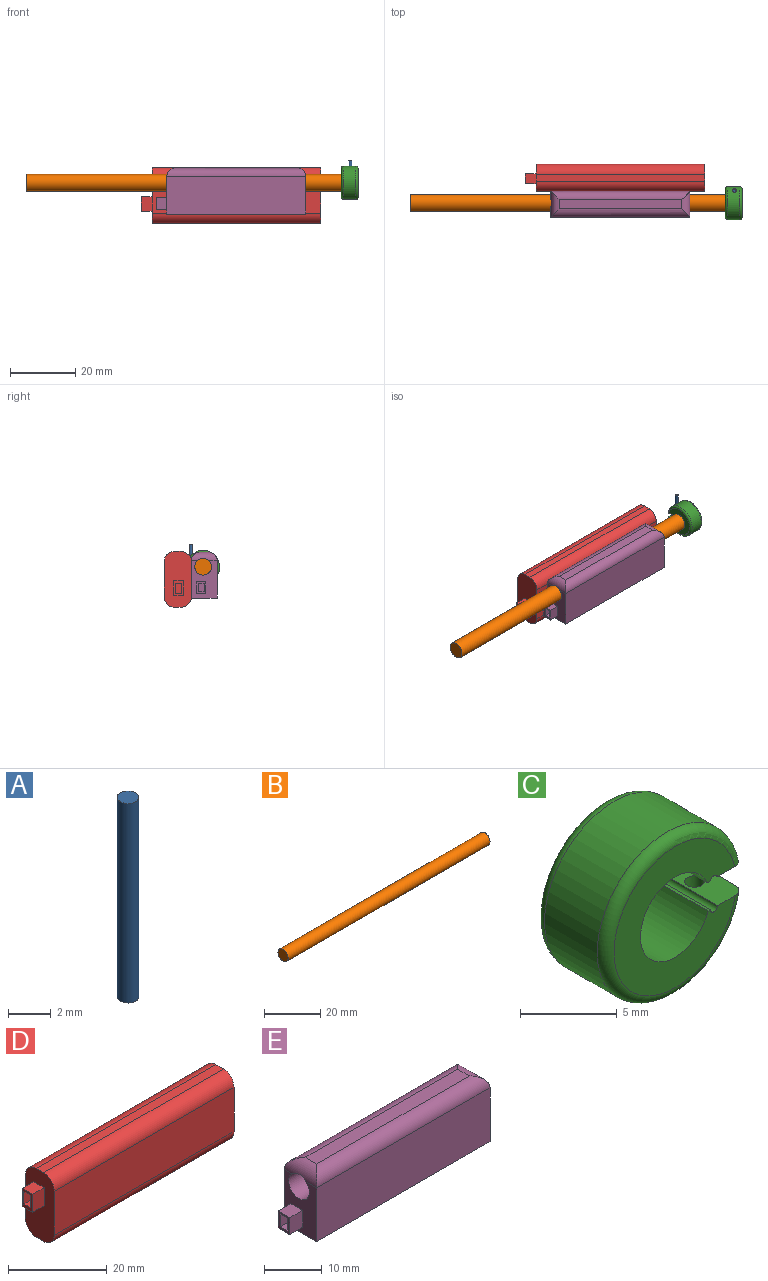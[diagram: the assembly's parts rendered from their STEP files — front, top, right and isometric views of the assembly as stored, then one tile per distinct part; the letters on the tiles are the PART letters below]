
ASSEMBLY  parts=5 mates=4
PART A: 3 faces, bbox 1x1x11.4 mm
  f0: cylinder r=0.51mm len=11.43mm, axis (0,0,-1), area 36.5mm2, adj f1,f2
  f1: plane 1.02x1.02mm, normal (0,0,1), area 0.8mm2, adj f0
  f2: plane 1.02x1.02mm, normal (0,0,-1), area 0.8mm2, adj f0
PART B: 3 faces, bbox 101.6x5.1x5.1 mm
  f0: cylinder r=2.54mm len=101.6mm, axis (-1,0,0), area 1621.5mm2, adj f1,f2
  f1: plane 5.08x5.08mm, normal (1,0,0), area 20.3mm2, adj f0
  f2: plane 5.08x5.08mm, normal (-1,0,0), area 20.3mm2, adj f0
PART C: 15 faces, bbox 10.9x5.1x11 mm
  f0: plane 5.08x1.89mm, normal (0,0,-1), area 8.6mm2, adj f1,f7,f8,f9,f11,f13,f14
  f1: cylinder r=5.08mm len=10.16mm, axis (0,1,0), area 112.8mm2, adj f0,f2,f10,f12,f13,f14
  f2: plane 5.08x1.92mm, normal (0,0,1), area 8.8mm2, adj f1,f3,f8,f9,f10,f13,f14
  f3: cylinder r=0.26mm len=5.08mm, axis (0,1,0), area 4.2mm2, adj f2,f4,f8,f9
  f4: plane 5.08x0.16mm, normal (0,0,1), area 0.8mm2, adj f3,f5,f8,f9
  f5: cylinder r=2.54mm len=5.08mm, axis (0,1,0), area 71.5mm2, adj f4,f6,f8,f9
  f6: plane 5.08x0.24mm, normal (0,0,-1), area 1.2mm2, adj f5,f7,f8,f9
  f7: cylinder r=0.27mm len=5.08mm, axis (0,1,0), area 3.6mm2, adj f0,f6,f8,f9
  f8: plane 8.93x8.86mm, normal (0,-1,0), area 38.6mm2, adj f0,f2,f3,f4,f5,f6,f7,f14
  f9: plane 8.93x8.86mm, normal (0,1,0), area 38.6mm2, adj f0,f2,f3,f4,f5,f6,f7,f13
  f10: cylinder r=0.51mm len=3.07mm, axis (0,0,1), area 8.1mm2, adj f1,f2
  f11: cylinder r=0.51mm len=2.84mm, axis (0,0,1), area 6.9mm2, adj f0,f12
  f12: bspline ~1.55x1.24mm, area 0.8mm2, adj f1,f11
  f13: torus R=4.47mm, axis (0,-1,0), area 27.6mm2, adj f0,f1,f2,f9
  f14: torus R=4.47mm, axis (0,-1,0), area 27.6mm2, adj f0,f1,f2,f8
PART D: 20 faces, bbox 54.9x8.3x17 mm
  f0: plane 17.05x8.27mm, normal (-1,0,0), area 119.4mm2, adj f1,f2,f3,f4,f6,f7,f8,f9
  f1: plane 51.56x2.14mm, normal (0,0,1), area 110.1mm2, adj f0,f5,f6,f9
  f2: plane 51.56x10.91mm, normal (0,-1,0), area 562.7mm2, adj f0,f5,f6,f7
  f3: plane 51.56x2.14mm, normal (0,0,-1), area 110.1mm2, adj f0,f5,f7,f8
  f4: plane 51.56x10.91mm, normal (0,1,0), area 562.7mm2, adj f0,f5,f8,f9
  f5: plane 17.05x8.27mm, normal (1,0,0), area 132.9mm2, adj f1,f2,f3,f4,f6,f7,f8,f9
  f6: cylinder r=3.07mm len=51.56mm, axis (-1,0,0), area 248.3mm2, adj f0,f1,f2,f5
  f7: cylinder r=3.07mm len=51.56mm, axis (1,0,0), area 248.3mm2, adj f0,f2,f3,f5
  f8: cylinder r=3.07mm len=51.56mm, axis (1,0,0), area 248.3mm2, adj f0,f3,f4,f5
  f9: cylinder r=3.07mm len=51.56mm, axis (-1,0,0), area 248.3mm2, adj f0,f1,f4,f5
  f10: plane 3.35x3.01mm, normal (0,0,-1), area 10.1mm2, adj f0,f11,f17,f18
  f11: plane 4.48x3.35mm, normal (0,1,0), area 15mm2, adj f0,f10,f12,f18
  f12: plane 3.35x3.01mm, normal (0,0,1), area 10.1mm2, adj f0,f11,f17,f18
  f13: plane 3.35x1.84mm, normal (0,0,-1), area 6.2mm2, adj f14,f16,f18,f19
  f14: plane 3.35x3.1mm, normal (0,-1,0), area 10.4mm2, adj f13,f15,f18,f19
  f15: plane 3.35x1.84mm, normal (0,0,1), area 6.2mm2, adj f14,f16,f18,f19
  f16: plane 3.35x3.1mm, normal (0,1,0), area 10.4mm2, adj f13,f15,f18,f19
  f17: plane 4.48x3.35mm, normal (0,-1,0), area 15mm2, adj f0,f10,f12,f18
  f18: plane 4.48x3.01mm, normal (-1,0,0), area 7.8mm2, adj f10,f11,f12,f13,f14,f15,f16,f17
  f19: plane 3.1x1.84mm, normal (-1,0,0), area 5.7mm2, adj f13,f14,f15,f16
PART E: 21 faces, bbox 45.7x7.9x14 mm
  f0: plane 42.58x11.43mm, normal (0,1,0), area 486.7mm2, adj f1,f3,f5,f7
  f1: plane 11.43x7.93mm, normal (-1,0,0), area 61.6mm2, adj f0,f2,f5,f6,f8,f11,f12,f13
  f2: plane 42.58x11.43mm, normal (0,-1,0), area 486.7mm2, adj f1,f3,f5,f10
  f3: plane 11.43x7.93mm, normal (1,0,0), area 72mm2, adj f0,f2,f5,f6,f9
  f4: plane 37.5x2.85mm, normal (0,0,1), area 107mm2, adj f7,f8,f9,f10
  f5: plane 42.58x7.93mm, normal (0,0,-1), area 337.8mm2, adj f0,f1,f2,f3
  f6: cylinder r=2.54mm len=42.58mm, axis (-1,0,0), area 679.2mm2, adj f1,f3,f8,f9
  f7: cylinder r=2.54mm len=42.58mm, axis (1,0,0), area 162.5mm2, adj f0,f4,f8,f9
  f8: cylinder r=2.54mm len=7.93mm, axis (0,1,0), area 22.7mm2, adj f1,f4,f6,f7,f10
  f9: cylinder r=2.54mm len=7.93mm, axis (0,-1,0), area 22.7mm2, adj f3,f4,f6,f7,f10
  f10: cylinder r=2.54mm len=42.58mm, axis (-1,0,0), area 162.5mm2, adj f2,f4,f8,f9
  f11: plane 3.6x3.15mm, normal (0,1,0), area 11.3mm2, adj f1,f12,f18,f19
  f12: plane 3.15x2.88mm, normal (0,0,1), area 9.1mm2, adj f1,f11,f13,f19
  f13: plane 3.6x3.15mm, normal (0,-1,0), area 11.3mm2, adj f1,f12,f18,f19
  f14: plane 3.15x1.8mm, normal (0,0,1), area 5.7mm2, adj f15,f17,f19,f20
  f15: plane 3.15x2.74mm, normal (0,1,0), area 8.6mm2, adj f14,f16,f19,f20
  f16: plane 3.15x1.8mm, normal (0,0,-1), area 5.7mm2, adj f15,f17,f19,f20
  f17: plane 3.15x2.74mm, normal (0,-1,0), area 8.6mm2, adj f14,f16,f19,f20
  f18: plane 3.15x2.88mm, normal (0,0,-1), area 9.1mm2, adj f1,f11,f13,f19
  f19: plane 3.6x2.88mm, normal (-1,0,0), area 5.4mm2, adj f11,f12,f13,f14,f15,f16,f17,f18
  f20: plane 2.74x1.8mm, normal (-1,0,0), area 4.9mm2, adj f14,f15,f16,f17
PLACE A t=(40.64,4.49,5.76)mm
PLACE B t=(-58.58,0.72,4.75)mm
PLACE C rot(axis=(0,0,1),90deg) t=(37.94,0.72,4.75)mm
PLACE D rot(axis=(1,0,0),180deg) t=(-19.97,12.59,9.43)mm
PLACE E t=(-15.48,-3.61,-4.81)mm fixed
MATE fastened C.f1 <-> B.f0  axis (-1,0,0) through (43.02,0.72,4.75)mm
MATE fastened D.f4 <-> E.f0  axis (0,-1,0) through (5.81,4.32,0.9)mm
MATE fastened A.f0 <-> C.f10  axis (0,0,-1) through (40.64,4.49,5.76)mm
MATE slider B.f0 <-> E.f6  axis (-1,0,0) through (-7.78,0.72,4.75)mm
